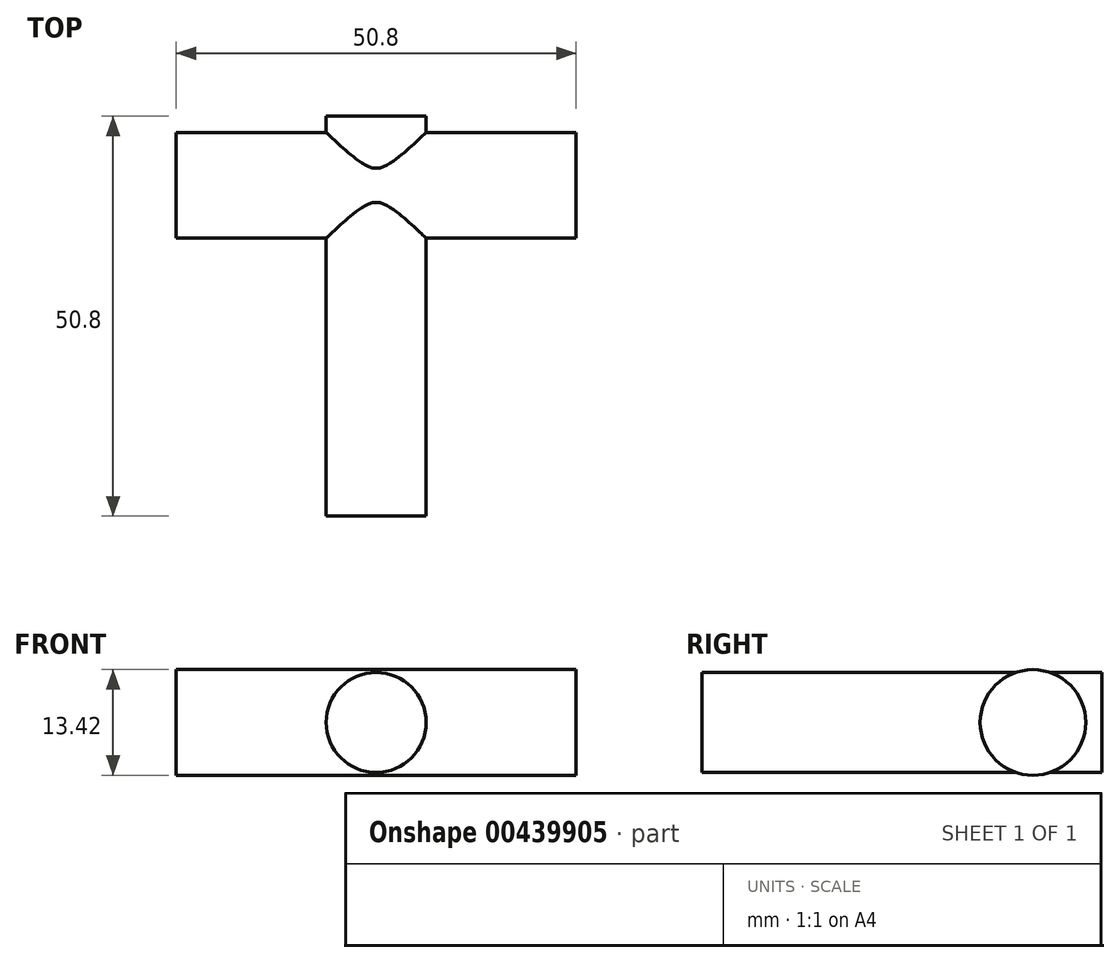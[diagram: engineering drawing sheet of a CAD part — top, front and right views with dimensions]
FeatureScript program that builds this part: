
annotation { "Feature Type Name" : "Feature", "Feature Type Description" : "" }
export const myFeature = defineFeature(function(context is Context, id is Id, definition is map)
    precondition{}
    {
        {
            var Q0;
            Q0=qCreatedBy(makeId("Front.planeOp"),FACE);
            var sketch = newSketch(context, id + "F0", { "sketchPlane" : qUnion([Q0])});
            skCircle(sketch, "E0", {"center": v(0, 0) * mm, "radius": 6.35 * mm});
            skSolve(sketch);
        }
        {
            var Q0;
            Q0=makeQuery(id+"F0.imprint","IMPRINT",FACE,{"disambiguationData":[TD([[makeQuery(id+"F0.imprint","IMPRINT",EDGE,{"derivedFrom":sQuery(id+"F0.wireOp",EDGE,"E0")}),1.0]])]});
            extrude(context, id + "F1", {"entities" : qUnion([Q0]), "depth" : 50.8 * mm});
        }
        {
            var Q0;
            Q0=qCreatedBy(makeId("Right.planeOp"),FACE);
            var sketch = newSketch(context, id + "F2", { "sketchPlane" : qUnion([Q0])});
            skCircle(sketch, "E1", {"center": v(-8.77, 0) * mm, "radius": 6.7 * mm});
            skSolve(sketch);
        }
        {
            var Q0;
            Q0 = qSketchRegion(id + "F2", true);
            extrude(context, id + "F3", {"entities" : qUnion([Q0]), "operationType" : NewBodyOperationType.ADD, "depth" : 25.4 * mm, "hasSecondDirection" : true, "secondDirectionOppositeDirection" : true, "secondDirectionDepth" : 25.4 * mm});
        }
    });
